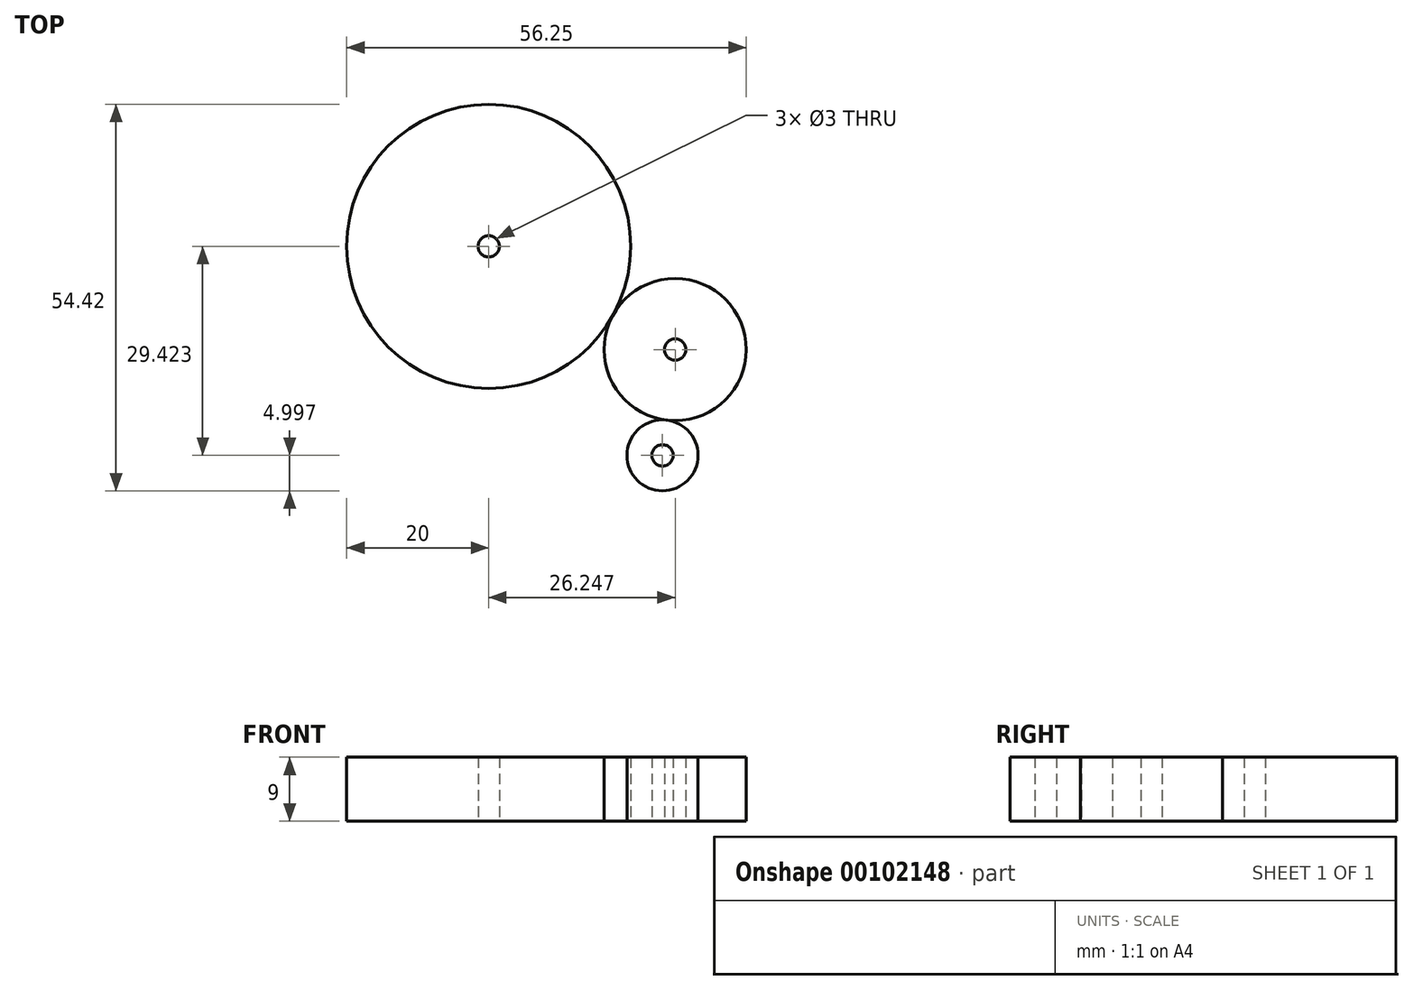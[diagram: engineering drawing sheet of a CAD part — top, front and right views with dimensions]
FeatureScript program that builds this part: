
annotation { "Feature Type Name" : "Feature", "Feature Type Description" : "" }
export const myFeature = defineFeature(function(context is Context, id is Id, definition is map)
    precondition{}
    {
        {
            var Q0;
            Q0=qCreatedBy(makeId("Top.planeOp"),FACE);
            var sketch = newSketch(context, id + "F0", { "sketchPlane" : qUnion([Q0])});
            skCircle(sketch, "E0", {"center": v(0, 0) * mm, "radius": 20 * mm});
            skLineSegment(sketch, "E1", {"start": v(0, 0) * mm, "end": v(26.25, -14.53) * mm});
            skLineSegment(sketch, "E2", {"start": v(26.25, -14.53) * mm, "end": v(0, 0) * mm});
            skCircle(sketch, "E3", {"center": v(26.25, -14.53) * mm, "radius": 10 * mm});
            skLineSegment(sketch, "E4", {"start": v(26.25, -14.53) * mm, "end": v(24.46, -29.42) * mm});
            skCircle(sketch, "E5", {"center": v(24.46, -29.42) * mm, "radius": 5 * mm});
            skLineSegment(sketch, "E6", {"start": v(-9.14, -17.8) * mm, "end": v(22.18, -33.87) * mm});
            skLineSegment(sketch, "E7", {"start": v(22.18, -33.87) * mm, "end": v(-9.14, -17.8) * mm});
            skLineSegment(sketch, "E8", {"start": v(28.94, -31.64) * mm, "end": v(35.21, -18.96) * mm});
            skLineSegment(sketch, "E9", {"start": v(35.21, -18.96) * mm, "end": v(28.94, -31.64) * mm});
            skLineSegment(sketch, "E10", {"start": v(14.96, 13.27) * mm, "end": v(33.73, -7.9) * mm});
            skLineSegment(sketch, "E11", {"start": v(33.73, -7.9) * mm, "end": v(14.96, 13.27) * mm});
            skCircle(sketch, "E12", {"center": v(0, 0) * mm, "radius": 1.5 * mm});
            skCircle(sketch, "E13", {"center": v(26.25, -14.53) * mm, "radius": 1.5 * mm});
            skCircle(sketch, "E14", {"center": v(24.46, -29.42) * mm, "radius": 1.5 * mm});
            skSolve(sketch);
        }
        {
            var Q0;
            Q0=makeQuery(id+"F0.imprint","IMPRINT",FACE,{"disambiguationData":[TD([[makeQuery(id+"F0.imprint","IMPRINT",EDGE,{"derivedFrom":sQuery(id+"F0.wireOp",EDGE,"E12")}),-1.0]])]});
            var Q1;
            {var subQ0=sQuery(id+"F0.wireOp",EDGE,"E11");Q1=makeQuery(id+"F0.imprint","IMPRINT",FACE,{"disambiguationData":[TD([[makeQuery(id+"F0.imprint","IMPRINT",EDGE,{"derivedFrom":subQ0}),1.0]])]});}
            var Q2;
            {var subQ0=sQuery(id+"F0.wireOp",EDGE,"E3");var subQ1=makeQuery(id+"F0.imprint","INTERSECT",VERTEX,{"derivedFrom":[subQ0,sQuery(id+"F0.wireOp",EDGE,"E9")]});Q2=makeQuery(id+"F0.imprint","IMPRINT",FACE,{"disambiguationData":[TD([[makeQuery(id+"F0.imprint","IMPRINT",EDGE,{"disambiguationData":[TD([[subQ1,-1.0]])],"derivedFrom":subQ0}),1.0]])]});}
            var Q3;
            {var subQ0=sQuery(id+"F0.wireOp",EDGE,"E13");var subQ1=sQuery(id+"F0.wireOp",EDGE,"E2");var subQ2=makeQuery(id+"F0.imprint","INTERSECT",VERTEX,{"derivedFrom":[subQ1,subQ0]});Q3=makeQuery(id+"F0.imprint","IMPRINT",FACE,{"disambiguationData":[TD([[makeQuery(id+"F0.imprint","IMPRINT",EDGE,{"disambiguationData":[TD([[subQ2,-1.0]])],"derivedFrom":subQ0}),-1.0]])]});}
            var Q4;
            {var subQ0=sQuery(id+"F0.wireOp",EDGE,"E7");Q4=makeQuery(id+"F0.imprint","IMPRINT",FACE,{"disambiguationData":[TD([[makeQuery(id+"F0.imprint","IMPRINT",EDGE,{"derivedFrom":subQ0}),-1.0]])]});}
            var Q5;
            {var subQ0=sQuery(id+"F0.wireOp",EDGE,"E9");Q5=makeQuery(id+"F0.imprint","IMPRINT",FACE,{"disambiguationData":[TD([[makeQuery(id+"F0.imprint","IMPRINT",EDGE,{"derivedFrom":subQ0}),-1.0]])]});}
            var Q6;
            Q6=makeQuery(id+"F0.imprint","IMPRINT",FACE,{"disambiguationData":[TD([[makeQuery(id+"F0.imprint","IMPRINT",EDGE,{"derivedFrom":sQuery(id+"F0.wireOp",EDGE,"E14")}),-1.0]])]});
            extrude(context, id + "F1", {"entities" : qUnion([Q0, Q1, Q2, Q3, Q4, Q5, Q6]), "depth" : 9 * mm});
        }
    });
